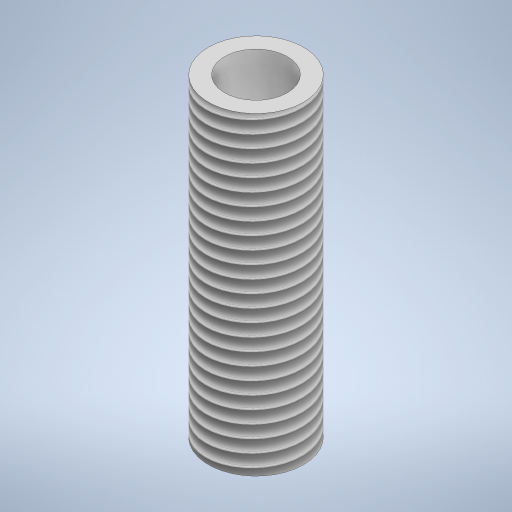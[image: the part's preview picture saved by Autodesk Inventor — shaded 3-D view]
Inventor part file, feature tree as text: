
AUTODESK INVENTOR PART (.ipt)
format: ipt  version: 2024 (Build 280153000, 153)  size: 315,904 bytes
history: native  units: mm
features: other x3, extrude x1, thread x1, hole x1
ambient origin geometry x8: Origin, YZ Plane, XZ Plane, XY Plane, X Axis, Y Axis, Z Axis, Center Point
bodies: Body1 (feature_tree)
feature tree (6):
  other  "Sólido1"
  extrude  "Extrusión1"  Depth=15.164mm
  thread  "Rosca1"  [1 undecoded]
  hole  "Agujero1"  [1 undecoded]
  other  "Edición directa1"
  other  "Escala1"
note: 2 required parameter values undecoded (feature->parameter linkage not recoverable at this tier; creation-order binding heuristic only, values carry confidence <= 0.55)
